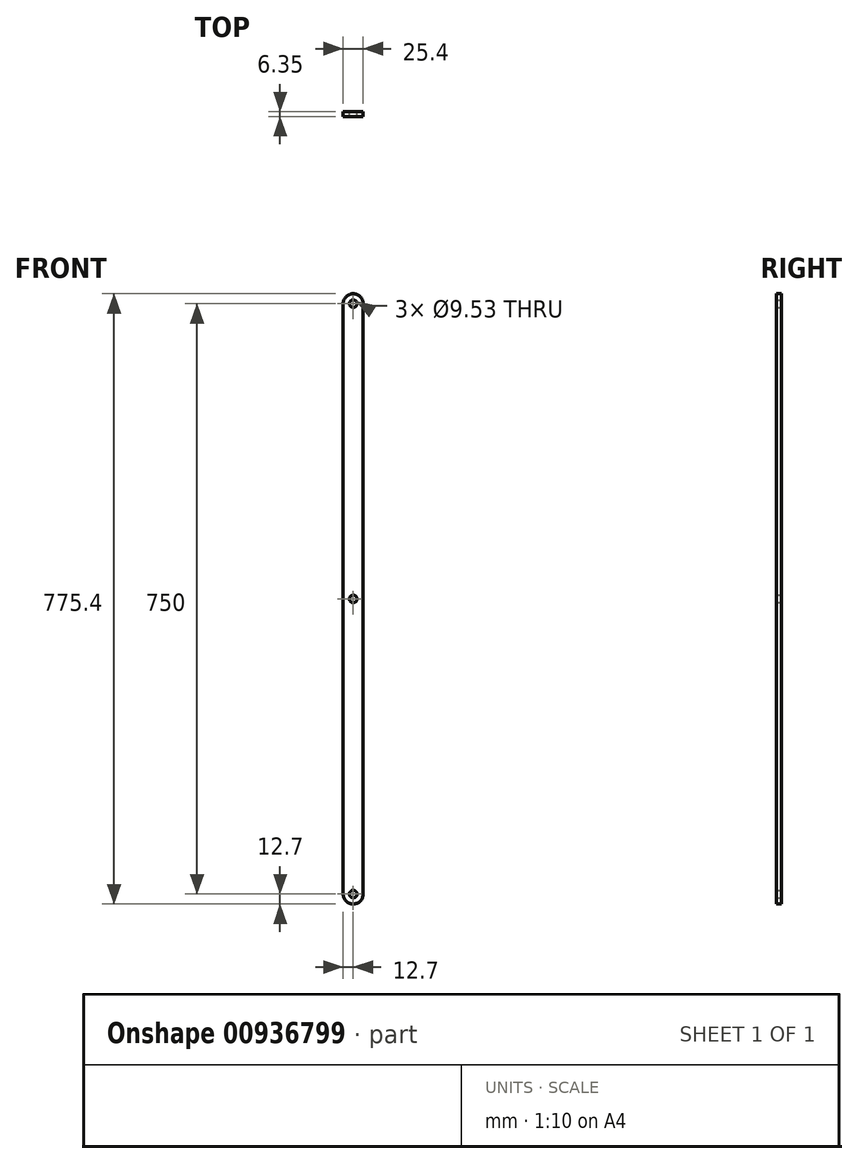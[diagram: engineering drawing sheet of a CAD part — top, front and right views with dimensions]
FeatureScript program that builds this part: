
annotation { "Feature Type Name" : "Feature", "Feature Type Description" : "" }
export const myFeature = defineFeature(function(context is Context, id is Id, definition is map)
    precondition{}
    {
        {
            var Q0;
            Q0=qCreatedBy(makeId("Front.planeOp"),FACE);
            var sketch = newSketch(context, id + "F0", { "sketchPlane" : qUnion([Q0])});
            skLineSegment(sketch, "E0", {"start": v(0, 0) * mm, "end": v(0, -750) * mm});
            skArc(sketch, "E1", {"start": v(0, -750) * mm, "mid": v(12.7, -762.7) * mm, "end": v(25.4, -750) * mm});
            skArc(sketch, "E2", {"start": v(0, 0) * mm, "mid": v(12.7, 12.7) * mm, "end": v(25.4, 0) * mm});
            skLineSegment(sketch, "E3", {"start": v(25.4, 0) * mm, "end": v(25.4, -750) * mm});
            skCircle(sketch, "E4", {"center": v(12.7, -750) * mm, "radius": 4.76 * mm});
            skCircle(sketch, "E5", {"center": v(12.7, 0) * mm, "radius": 4.76 * mm});
            skCircle(sketch, "E6", {"center": v(12.7, -375) * mm, "radius": 4.76 * mm});
            skPoint(sketch, "E6.centerSnap0", {"position": v(25.4, -375) * mm});
            skSolve(sketch);
        }
        {
            var Q0;
            Q0=makeQuery(id+"F0.imprint","IMPRINT",FACE,{"disambiguationData":[TD([[makeQuery(id+"F0.imprint","IMPRINT",EDGE,{"derivedFrom":sQuery(id+"F0.wireOp",EDGE,"E0")}),1.0]])]});
            extrude(context, id + "F1", {"entities" : qUnion([Q0]), "depth" : 6.35 * mm});
        }
    });
